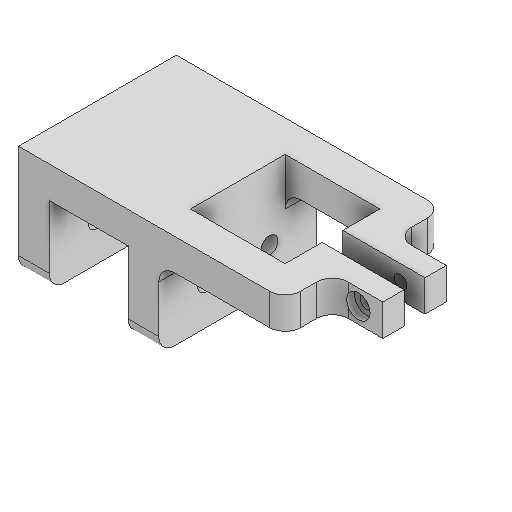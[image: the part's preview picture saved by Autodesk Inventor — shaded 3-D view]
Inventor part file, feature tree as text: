
AUTODESK INVENTOR PART (.ipt)
format: ipt  version: 2025 (Build 290162000, 162)  size: 211,456 bytes
history: native  units: mm
features: extrude x5, sketch x5, projected_geometry x3, fillet x1
ambient origin geometry x8: Origin, YZ Plane, XZ Plane, XY Plane, X Axis, Y Axis, Z Axis, Center Point
bodies: Solid1 (feature_tree)
feature tree (14):
  extrude  "Extrusion1"  Depth=30.0mm
  extrude  "Extrusion2"  Depth=10.0mm
  extrude  "Extrusion3"  Depth=10.0mm
  fillet  "Fillet1"  Radius=25.0mm
  extrude  "Extrusion4"  Depth=2.7mm
  extrude  "Extrusion5"  Depth=10.0mm
  sketch  "Sketch1"  dims[d0=30.0mm d1=30.0mm]
  sketch  "Sketch2"  dims[d2=10.0mm d4=44.45mm]
  projected_geometry  "Projected Loop1"
  sketch  "Sketch3"  dims[d5=10.0mm d6=0.0mm d7=25.0mm d8=25.0mm d9=0.0mm]
  projected_geometry  "Projected Loop2"
  sketch  "Sketch4"  dims[d10=20.0mm d11=2.7mm]
  projected_geometry  "Projected Loop3"
  sketch  "Sketch5"  dims[d12=0.0mm d13=0.0mm d14=5.0mm d15=4.0mm d16=10.0mm d17=0.0mm d18=5.0mm d19=0.0mm]
